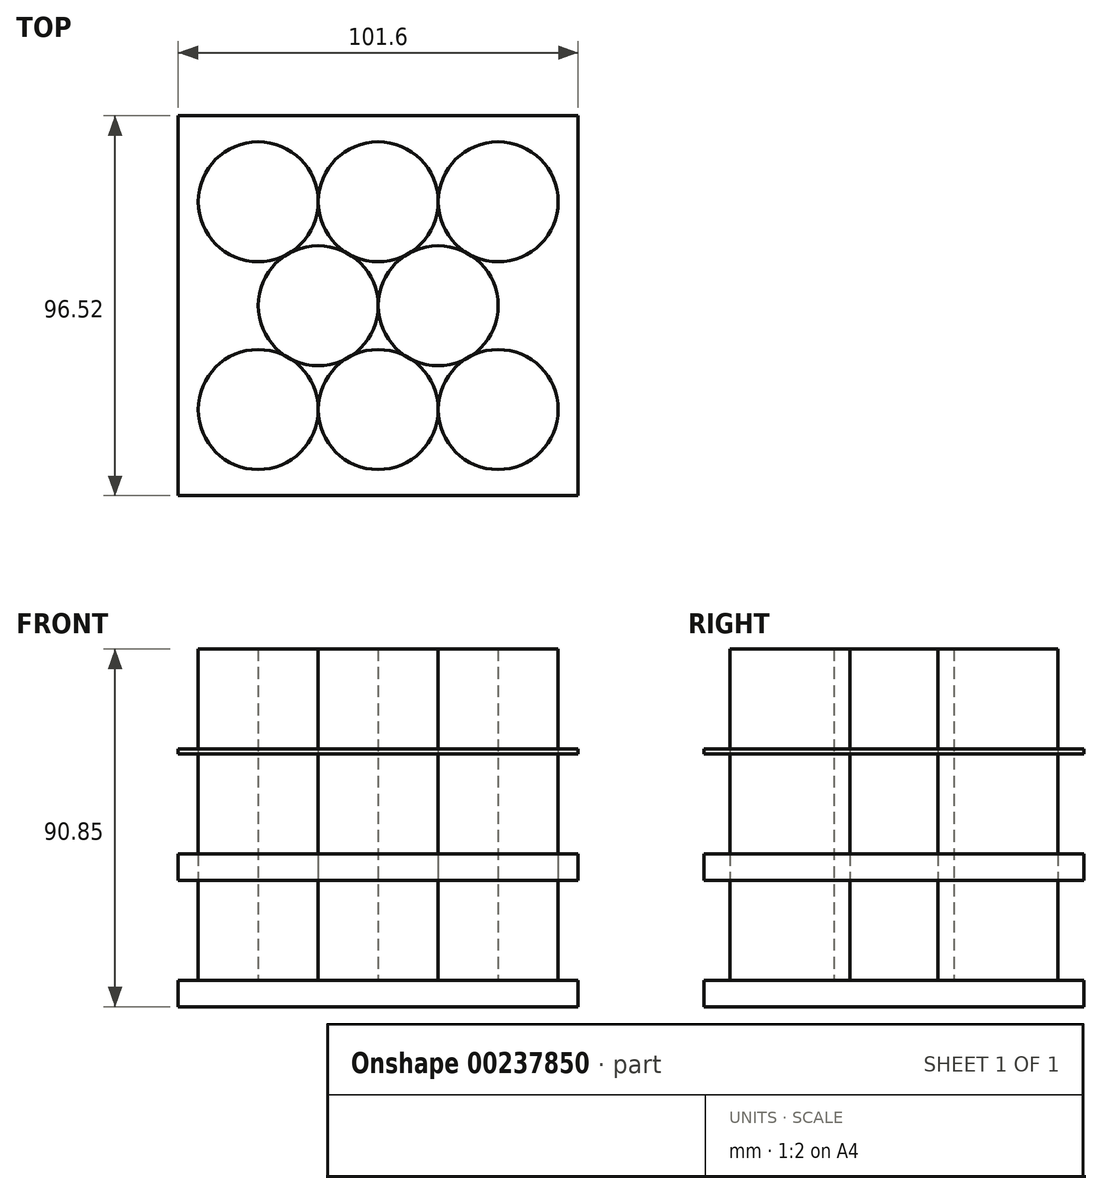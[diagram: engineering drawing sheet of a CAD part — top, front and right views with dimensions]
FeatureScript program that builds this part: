
annotation { "Feature Type Name" : "Feature", "Feature Type Description" : "" }
export const myFeature = defineFeature(function(context is Context, id is Id, definition is map)
    precondition{}
    {
        {
            var Q0;
            Q0=qCreatedBy(makeId("Top.planeOp"),FACE);
            var sketch = newSketch(context, id + "F0", { "sketchPlane" : qUnion([Q0])});
            skCircle(sketch, "E0", {"center": v(-30.48, -26.4) * mm, "radius": 15.24 * mm});
            skCircle(sketch, "E1", {"center": v(0, -26.4) * mm, "radius": 15.24 * mm});
            skCircle(sketch, "E2", {"center": v(-15.24, 0) * mm, "radius": 15.24 * mm});
            skCircle(sketch, "E3", {"center": v(-30.48, 26.4) * mm, "radius": 15.24 * mm});
            skCircle(sketch, "E4", {"center": v(0, 26.4) * mm, "radius": 15.24 * mm});
            skCircle(sketch, "E5", {"center": v(30.48, -26.4) * mm, "radius": 15.24 * mm});
            skCircle(sketch, "E6", {"center": v(15.24, 0) * mm, "radius": 15.24 * mm});
            skCircle(sketch, "E7", {"center": v(30.48, 26.4) * mm, "radius": 15.24 * mm});
            skLineSegment(sketch, "E8", {"start": v(0, 26.4) * mm, "end": v(30.48, -26.4) * mm, "construction": true});
            skLineSegment(sketch, "E9", {"start": v(0, 26.4) * mm, "end": v(0, -26.4) * mm, "construction": true});
            skSolve(sketch);
        }
        {
            var Q0;
            {var subQ0=sQuery(id+"F0.wireOp",EDGE,"ICpDPUjX-ivMe-23Ei-ieje-qIsjfVPonkm3");var subQ1=makeQuery(id+"F0.imprint","INTERSECT",VERTEX,{"derivedFrom":[subQ0,sQuery(id+"F0.wireOp",EDGE,"1585de0c-b4fc-4455-9636-1ccd38715f07")]});Q0=makeQuery(id+"F0.imprint","IMPRINT",FACE,{"disambiguationData":[TD([[makeQuery(id+"F0.imprint","IMPRINT",EDGE,{"disambiguationData":[TD([[subQ1,-1.0]])],"derivedFrom":subQ0}),1.0]])]});}
            var Q1;
            {var subQ0=sQuery(id+"F0.wireOp",EDGE,"1585de0c-b4fc-4455-9636-1ccd38715f07");var subQ1=makeQuery(id+"F0.imprint","INTERSECT",VERTEX,{"derivedFrom":[sQuery(id+"F0.wireOp",EDGE,"ICpDPUjX-ivMe-23Ei-ieje-qIsjfVPonkm3"),subQ0]});Q1=makeQuery(id+"F0.imprint","IMPRINT",FACE,{"disambiguationData":[TD([[makeQuery(id+"F0.imprint","IMPRINT",EDGE,{"disambiguationData":[TD([[subQ1,1.0]])],"derivedFrom":subQ0}),1.0]])]});}
            var Q2;
            {var subQ0=sQuery(id+"F0.wireOp",EDGE,"8cf919d0-c88a-4376-973f-18324e1bfcb2");var subQ1=makeQuery(id+"F0.imprint","INTERSECT",VERTEX,{"derivedFrom":[sQuery(id+"F0.wireOp",EDGE,"1585de0c-b4fc-4455-9636-1ccd38715f07"),subQ0]});Q2=makeQuery(id+"F0.imprint","IMPRINT",FACE,{"disambiguationData":[TD([[makeQuery(id+"F0.imprint","IMPRINT",EDGE,{"disambiguationData":[TD([[subQ1,-1.0]])],"derivedFrom":subQ0}),1.0]])]});}
            var Q3;
            {var subQ0=sQuery(id+"F0.wireOp",EDGE,"0c448a11-c32a-4d7b-bc3d-f4b18554e8e6");var subQ1=makeQuery(id+"F0.imprint","INTERSECT",VERTEX,{"derivedFrom":[sQuery(id+"F0.wireOp",EDGE,"8cf919d0-c88a-4376-973f-18324e1bfcb2"),subQ0]});Q3=makeQuery(id+"F0.imprint","IMPRINT",FACE,{"disambiguationData":[TD([[makeQuery(id+"F0.imprint","IMPRINT",EDGE,{"disambiguationData":[TD([[subQ1,-1.0]])],"derivedFrom":subQ0}),1.0]])]});}
            var Q4;
            {var subQ0=sQuery(id+"F0.wireOp",EDGE,"877ee094-fdc9-495d-ab0e-c5a52c05f9cd");var subQ4=makeQuery(id+"F0.imprint","INTERSECT",VERTEX,{"derivedFrom":[sQuery(id+"F0.wireOp",EDGE,"8cf919d0-c88a-4376-973f-18324e1bfcb2"),subQ0]});Q4=makeQuery(id+"F0.imprint","IMPRINT",FACE,{"disambiguationData":[TD([[makeQuery(id+"F0.imprint","IMPRINT",EDGE,{"disambiguationData":[TD([[subQ4,1.0]])],"derivedFrom":subQ0}),1.0]])]});}
            var Q5;
            {var subQ0=sQuery(id+"F0.wireOp",EDGE,"d8245553-00ec-417b-91d8-0db8256ae251");var subQ4=makeQuery(id+"F0.imprint","INTERSECT",VERTEX,{"derivedFrom":[sQuery(id+"F0.wireOp",EDGE,"1585de0c-b4fc-4455-9636-1ccd38715f07"),subQ0]});Q5=makeQuery(id+"F0.imprint","IMPRINT",FACE,{"disambiguationData":[TD([[makeQuery(id+"F0.imprint","IMPRINT",EDGE,{"disambiguationData":[TD([[subQ4,1.0]])],"derivedFrom":subQ0}),1.0]])]});}
            var Q6;
            {var subQ0=sQuery(id+"F0.wireOp",EDGE,"5c829891-7c72-403d-9d87-70b6dc1f70b6");var subQ1=makeQuery(id+"F0.imprint","INTERSECT",VERTEX,{"derivedFrom":[sQuery(id+"F0.wireOp",EDGE,"d8245553-00ec-417b-91d8-0db8256ae251"),subQ0]});Q6=makeQuery(id+"F0.imprint","IMPRINT",FACE,{"disambiguationData":[TD([[makeQuery(id+"F0.imprint","IMPRINT",EDGE,{"disambiguationData":[TD([[subQ1,1.0]])],"derivedFrom":subQ0}),1.0]])]});}
            var Q7;
            {var subQ0=sQuery(id+"F0.wireOp",EDGE,"E0");var subQ1=makeQuery(id+"F0.imprint","INTERSECT",VERTEX,{"derivedFrom":[subQ0,sQuery(id+"F0.wireOp",EDGE,"E1")]});Q7=makeQuery(id+"F0.imprint","IMPRINT",FACE,{"disambiguationData":[TD([[makeQuery(id+"F0.imprint","IMPRINT",EDGE,{"disambiguationData":[TD([[subQ1,-1.0]])],"derivedFrom":subQ0}),1.0]])]});}
            var Q8;
            {var subQ0=sQuery(id+"F0.wireOp",EDGE,"E1");var subQ1=makeQuery(id+"F0.imprint","INTERSECT",VERTEX,{"derivedFrom":[sQuery(id+"F0.wireOp",EDGE,"0c448a11-c32a-4d7b-bc3d-f4b18554e8e6"),subQ0]});Q8=makeQuery(id+"F0.imprint","IMPRINT",FACE,{"disambiguationData":[TD([[makeQuery(id+"F0.imprint","IMPRINT",EDGE,{"disambiguationData":[TD([[subQ1,-1.0]])],"derivedFrom":subQ0}),1.0]])]});}
            var Q9;
            {var subQ0=sQuery(id+"F0.wireOp",EDGE,"0cc3aad7-621e-4e71-9b65-14e129a84a9b");var subQ1=makeQuery(id+"F0.imprint","INTERSECT",VERTEX,{"derivedFrom":[sQuery(id+"F0.wireOp",EDGE,"5c829891-7c72-403d-9d87-70b6dc1f70b6"),subQ0]});Q9=makeQuery(id+"F0.imprint","IMPRINT",FACE,{"disambiguationData":[TD([[makeQuery(id+"F0.imprint","IMPRINT",EDGE,{"disambiguationData":[TD([[subQ1,1.0]])],"derivedFrom":subQ0}),1.0]])]});}
            var Q10;
            {var subQ0=sQuery(id+"F0.wireOp",EDGE,"bd5ddfc4-a346-494c-b61b-99bb20945c8d");var subQ1=makeQuery(id+"F0.imprint","INTERSECT",VERTEX,{"derivedFrom":[sQuery(id+"F0.wireOp",EDGE,"0cc3aad7-621e-4e71-9b65-14e129a84a9b"),subQ0]});Q10=makeQuery(id+"F0.imprint","IMPRINT",FACE,{"disambiguationData":[TD([[makeQuery(id+"F0.imprint","IMPRINT",EDGE,{"disambiguationData":[TD([[subQ1,1.0]])],"derivedFrom":subQ0}),1.0]])]});}
            var Q11;
            {var subQ0=sQuery(id+"F0.wireOp",EDGE,"E2");var subQ1=makeQuery(id+"F0.imprint","INTERSECT",VERTEX,{"derivedFrom":[sQuery(id+"F0.wireOp",EDGE,"E1"),subQ0]});Q11=makeQuery(id+"F0.imprint","IMPRINT",FACE,{"disambiguationData":[TD([[makeQuery(id+"F0.imprint","IMPRINT",EDGE,{"disambiguationData":[TD([[subQ1,1.0]])],"derivedFrom":subQ0}),1.0]])]});}
            var Q12;
            Q12=makeQuery(id+"F0.imprint","IMPRINT",FACE,{"disambiguationData":[TD([[makeQuery(id+"F0.imprint","IMPRINT",EDGE,{"derivedFrom":sQuery(id+"F0.wireOp",EDGE,"E7")}),1.0]])]});
            var Q13;
            {var subQ0=sQuery(id+"F0.wireOp",EDGE,"E5");var subQ1=makeQuery(id+"F0.imprint","INTERSECT",VERTEX,{"derivedFrom":[sQuery(id+"F0.wireOp",EDGE,"E1"),subQ0]});Q13=makeQuery(id+"F0.imprint","IMPRINT",FACE,{"disambiguationData":[TD([[makeQuery(id+"F0.imprint","IMPRINT",EDGE,{"disambiguationData":[TD([[subQ1,1.0]])],"derivedFrom":subQ0}),1.0]])]});}
            var Q14;
            {var subQ0=sQuery(id+"F0.wireOp",EDGE,"E3");var subQ1=makeQuery(id+"F0.imprint","INTERSECT",VERTEX,{"derivedFrom":[sQuery(id+"F0.wireOp",EDGE,"25d6187e-9874-44d9-9059-f21ffbd7d0e7"),subQ0]});Q14=makeQuery(id+"F0.imprint","IMPRINT",FACE,{"disambiguationData":[TD([[makeQuery(id+"F0.imprint","IMPRINT",EDGE,{"disambiguationData":[TD([[subQ1,1.0]])],"derivedFrom":subQ0}),1.0]])]});}
            var Q15;
            {var subQ0=sQuery(id+"F0.wireOp",EDGE,"25d6187e-9874-44d9-9059-f21ffbd7d0e7");var subQ1=makeQuery(id+"F0.imprint","INTERSECT",VERTEX,{"derivedFrom":[sQuery(id+"F0.wireOp",EDGE,"0cc3aad7-621e-4e71-9b65-14e129a84a9b"),subQ0]});Q15=makeQuery(id+"F0.imprint","IMPRINT",FACE,{"disambiguationData":[TD([[makeQuery(id+"F0.imprint","IMPRINT",EDGE,{"disambiguationData":[TD([[subQ1,1.0]])],"derivedFrom":subQ0}),1.0]])]});}
            var Q16;
            {var subQ0=sQuery(id+"F0.wireOp",EDGE,"E6");var subQ1=makeQuery(id+"F0.imprint","INTERSECT",VERTEX,{"derivedFrom":[subQ0,sQuery(id+"F0.wireOp",EDGE,"E7")]});Q16=makeQuery(id+"F0.imprint","IMPRINT",FACE,{"disambiguationData":[TD([[makeQuery(id+"F0.imprint","IMPRINT",EDGE,{"disambiguationData":[TD([[subQ1,-1.0]])],"derivedFrom":subQ0}),1.0]])]});}
            var Q17;
            {var subQ0=sQuery(id+"F0.wireOp",EDGE,"E4");var subQ1=makeQuery(id+"F0.imprint","INTERSECT",VERTEX,{"derivedFrom":[sQuery(id+"F0.wireOp",EDGE,"E3"),subQ0]});Q17=makeQuery(id+"F0.imprint","IMPRINT",FACE,{"disambiguationData":[TD([[makeQuery(id+"F0.imprint","IMPRINT",EDGE,{"disambiguationData":[TD([[subQ1,1.0]])],"derivedFrom":subQ0}),1.0]])]});}
            var Q18;
            Q18=sQuery(id+"F0.wireOp",EDGE,"877ee094-fdc9-495d-ab0e-c5a52c05f9cd");
            var Q19;
            Q19=sQuery(id+"F0.wireOp",EDGE,"ICpDPUjX-ivMe-23Ei-ieje-qIsjfVPonkm3");
            var Q20;
            Q20=sQuery(id+"F0.wireOp",EDGE,"E1");
            var Q21;
            Q21=sQuery(id+"F0.wireOp",EDGE,"E0");
            var Q22;
            Q22=sQuery(id+"F0.wireOp",EDGE,"5c829891-7c72-403d-9d87-70b6dc1f70b6");
            var Q23;
            Q23=sQuery(id+"F0.wireOp",EDGE,"0c448a11-c32a-4d7b-bc3d-f4b18554e8e6");
            var Q24;
            Q24=sQuery(id+"F0.wireOp",EDGE,"d8245553-00ec-417b-91d8-0db8256ae251");
            var Q25;
            Q25=sQuery(id+"F0.wireOp",EDGE,"8cf919d0-c88a-4376-973f-18324e1bfcb2");
            var Q26;
            Q26=sQuery(id+"F0.wireOp",EDGE,"1585de0c-b4fc-4455-9636-1ccd38715f07");
            extrude(context, id + "F1", {"entities" : qUnion([Q0, Q1, Q2, Q3, Q4, Q5, Q6, Q7, Q8, Q9, Q10, Q11, Q12, Q13, Q14, Q15, Q16, Q17]), "surfaceEntities" : qUnion([Q18, Q19, Q20, Q21, Q22, Q23, Q24, Q25, Q26]), "depth" : 84.16 * mm});
        }
        {
            var Q0;
            Q0=qCreatedBy(makeId("Front.planeOp"),FACE);
            var sketch = newSketch(context, id + "F2", { "sketchPlane" : qUnion([Q0])});
            skLineSegment(sketch, "E10.bottom", {"start": v(50.8, 0) * mm, "end": v(-50.8, 0) * mm});
            skLineSegment(sketch, "E10.top", {"start": v(50.8, -6.7) * mm, "end": v(-50.8, -6.7) * mm});
            skLineSegment(sketch, "E10.left", {"start": v(50.8, 0) * mm, "end": v(50.8, -6.7) * mm});
            skLineSegment(sketch, "E10.right", {"start": v(-50.8, 0) * mm, "end": v(-50.8, -6.7) * mm});
            skLineSegment(sketch, "E11", {"start": v(-45.8, 25.4) * mm, "end": v(45.84, 25.4) * mm, "construction": true});
            skLineSegment(sketch, "E12.bottom", {"start": v(50.8, 32.1) * mm, "end": v(-50.8, 32.1) * mm});
            skLineSegment(sketch, "E12.top", {"start": v(50.8, 25.4) * mm, "end": v(-50.8, 25.4) * mm});
            skLineSegment(sketch, "E12.left", {"start": v(50.8, 32.1) * mm, "end": v(50.8, 25.4) * mm});
            skLineSegment(sketch, "E12.right", {"start": v(-50.8, 32.1) * mm, "end": v(-50.8, 25.4) * mm});
            skLineSegment(sketch, "E13", {"start": v(50.8, -6.7) * mm, "end": v(50.8, 25.4) * mm, "construction": true});
            skLineSegment(sketch, "E14.bottom", {"start": v(50.8, 58.76) * mm, "end": v(-50.8, 58.76) * mm});
            skLineSegment(sketch, "E14.top", {"start": v(50.8, 57.5) * mm, "end": v(-50.8, 57.5) * mm});
            skLineSegment(sketch, "E14.left", {"start": v(50.8, 58.76) * mm, "end": v(50.8, 57.5) * mm});
            skLineSegment(sketch, "E14.right", {"start": v(-50.8, 58.76) * mm, "end": v(-50.8, 57.5) * mm});
            skLineSegment(sketch, "E15", {"start": v(-50.8, 58.76) * mm, "end": v(-50.8, 32.1) * mm, "construction": true});
            skSolve(sketch);
        }
        {
            var Q0;
            Q0=makeQuery(id+"F2.imprint","IMPRINT",FACE,{"disambiguationData":[TD([[makeQuery(id+"F2.imprint","IMPRINT",EDGE,{"derivedFrom":sQuery(id+"F2.wireOp",EDGE,"E10.bottom")}),1.0]])]});
            var Q1;
            Q1=makeQuery(id+"F2.imprint","IMPRINT",FACE,{"disambiguationData":[TD([[makeQuery(id+"F2.imprint","IMPRINT",EDGE,{"derivedFrom":sQuery(id+"F2.wireOp",EDGE,"E12.bottom")}),1.0]])]});
            var Q2;
            Q2=makeQuery(id+"F2.imprint","IMPRINT",FACE,{"disambiguationData":[TD([[makeQuery(id+"F2.imprint","IMPRINT",EDGE,{"derivedFrom":sQuery(id+"F2.wireOp",EDGE,"E14.bottom")}),1.0]])]});
            var Q3;
            Q3=sQuery(id+"F2.wireOp",EDGE,"E10.bottom");
            extrude(context, id + "F3", {"entities" : qUnion([Q0, Q1, Q2]), "surfaceEntities" : qUnion([Q3]), "endBound" : BoundingType.SYMMETRIC, "oppositeDirection" : true, "depth" : 96.52 * mm});
        }
    });
